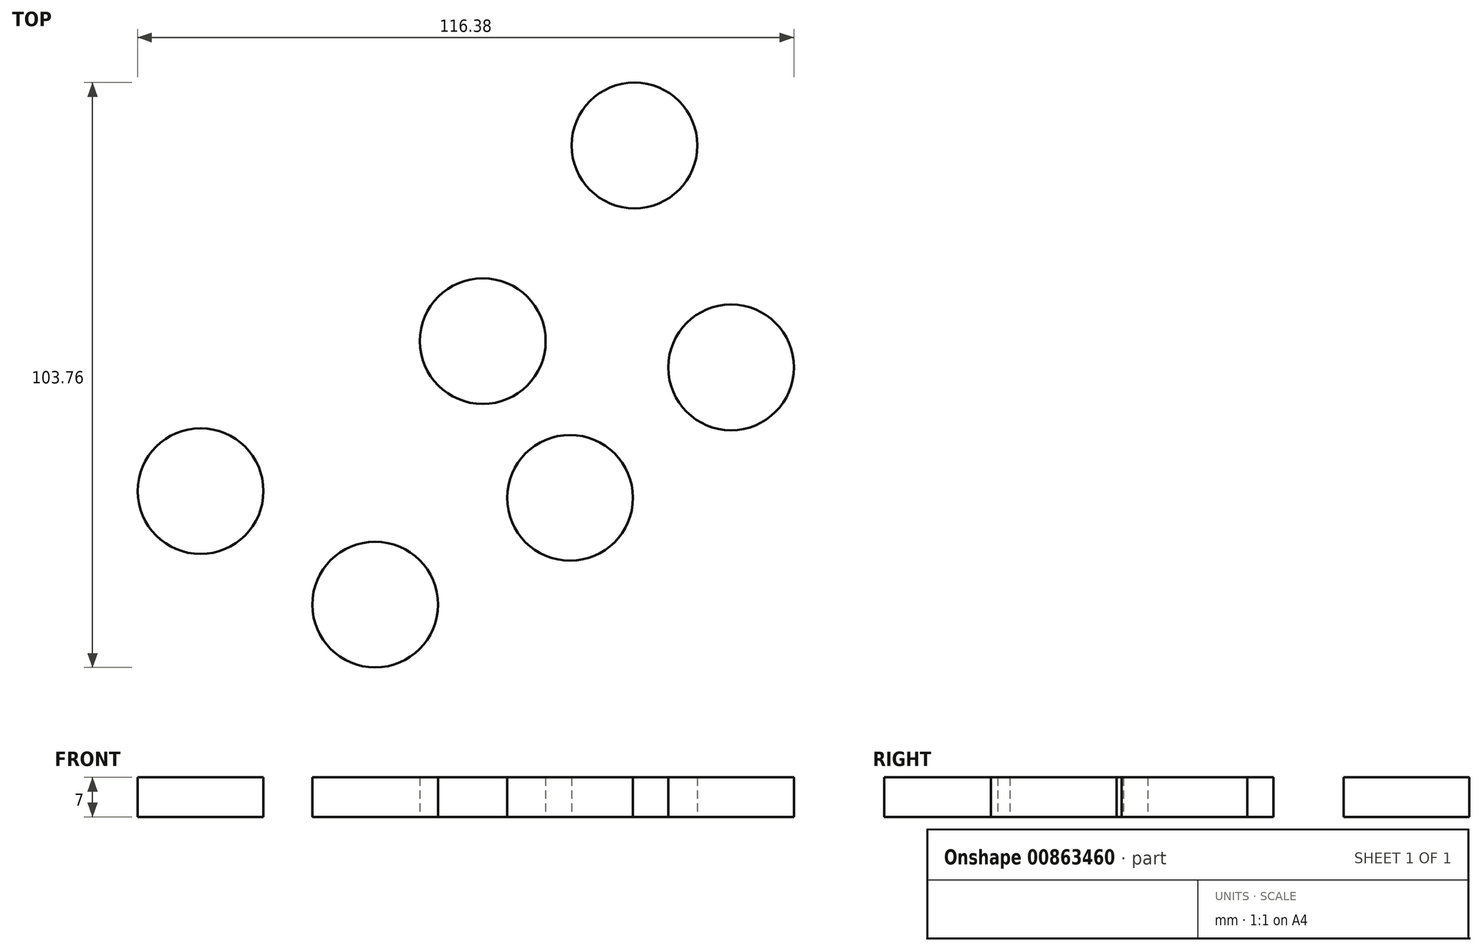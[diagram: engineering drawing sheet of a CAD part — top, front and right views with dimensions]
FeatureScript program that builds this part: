
annotation { "Feature Type Name" : "Feature", "Feature Type Description" : "" }
export const myFeature = defineFeature(function(context is Context, id is Id, definition is map)
    precondition{}
    {
        {
            var Q0;
            Q0=qCreatedBy(makeId("Top.planeOp"),FACE);
            var sketch = newSketch(context, id + "F0", { "sketchPlane" : qUnion([Q0])});
            skCircle(sketch, "E0", {"center": v(0, 0) * mm, "radius": 11.15 * mm});
            skCircle(sketch, "E1", {"center": v(26.9, 34.72) * mm, "radius": 11.15 * mm});
            skCircle(sketch, "E2", {"center": v(-50.05, -26.6) * mm, "radius": 11.15 * mm});
            skCircle(sketch, "E3", {"center": v(-19.09, -46.74) * mm, "radius": 11.15 * mm});
            skCircle(sketch, "E4", {"center": v(15.48, -27.8) * mm, "radius": 11.15 * mm});
            skCircle(sketch, "E5", {"center": v(44.03, -4.66) * mm, "radius": 11.15 * mm});
            skSolve(sketch);
        }
        {
            var Q0;
            Q0 = qSketchRegion(id + "F0", true);
            extrude(context, id + "F1", {"entities" : qUnion([Q0]), "depth" : 7 * mm, "offsetDistance" : 25 * mm});
        }
    });
